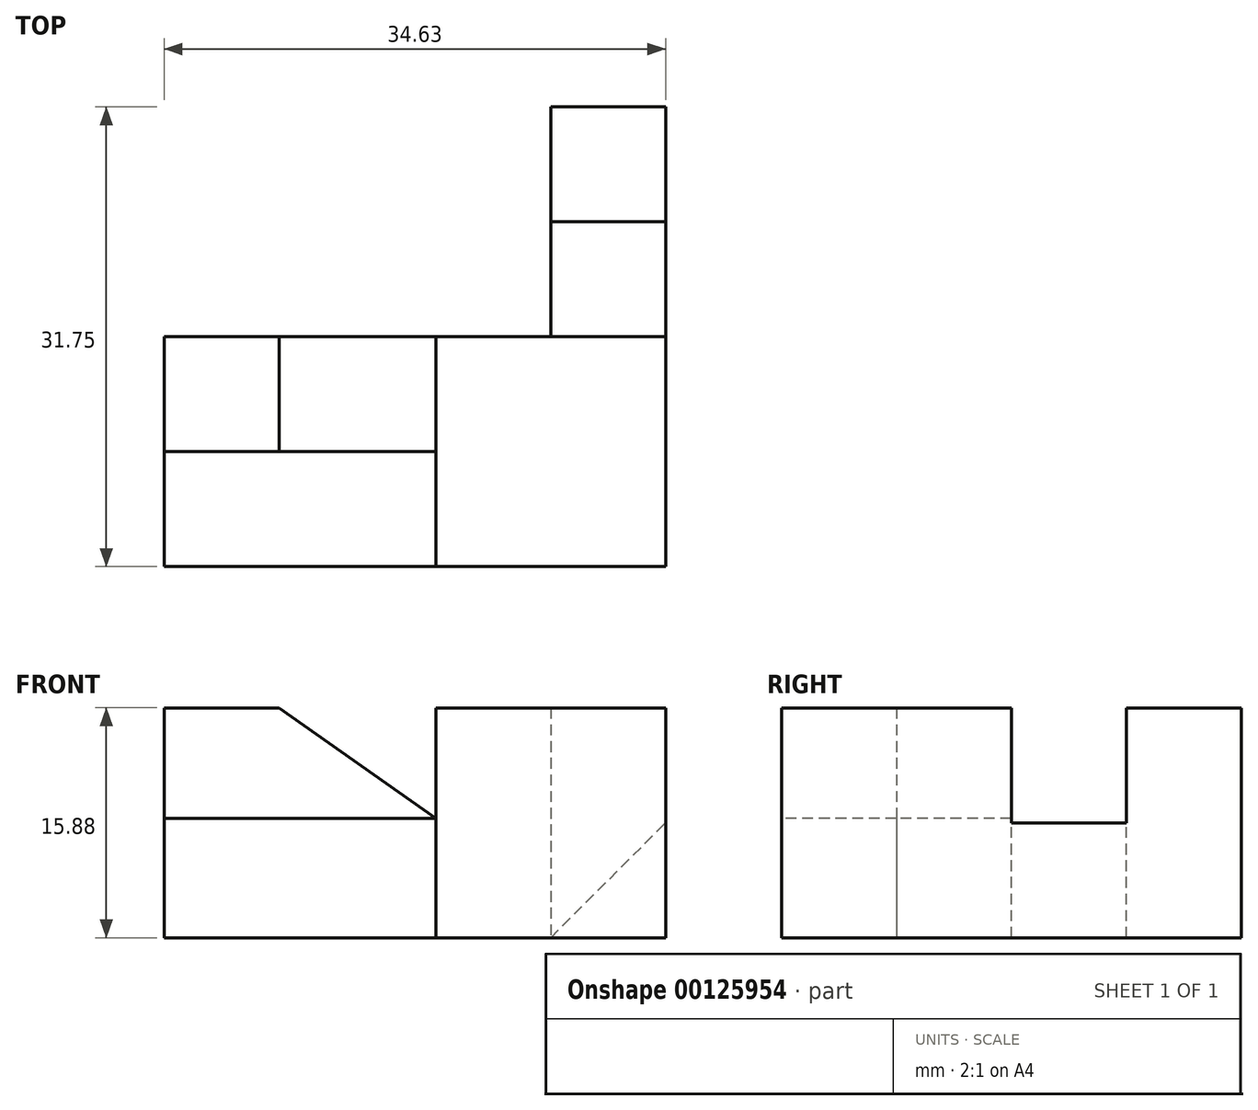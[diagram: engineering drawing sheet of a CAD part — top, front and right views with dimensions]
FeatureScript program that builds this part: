
annotation { "Feature Type Name" : "Feature", "Feature Type Description" : "" }
export const myFeature = defineFeature(function(context is Context, id is Id, definition is map)
    precondition{}
    {
        {
            var Q0;
            Q0=qCreatedBy(makeId("Top.planeOp"),FACE);
            var sketch = newSketch(context, id + "F0", { "sketchPlane" : qUnion([Q0])});
            skLineSegment(sketch, "E0.bottom", {"start": v(0, 0) * mm, "end": v(34.63, 0) * mm});
            skLineSegment(sketch, "E0.right", {"start": v(34.63, 0) * mm, "end": v(34.63, 31.75) * mm});
            skLineSegment(sketch, "E1", {"start": v(0, 15.88) * mm, "end": v(34.63, 15.88) * mm});
            skLineSegment(sketch, "E2", {"start": v(7.94, 15.88) * mm, "end": v(7.94, 7.94) * mm});
            skLineSegment(sketch, "E3", {"start": v(0, 15.88) * mm, "end": v(0, 0) * mm});
            skLineSegment(sketch, "E4", {"start": v(26.7, 31.75) * mm, "end": v(34.63, 31.75) * mm});
            skLineSegment(sketch, "E5", {"start": v(26.7, 23.81) * mm, "end": v(34.63, 23.81) * mm});
            skLineSegment(sketch, "E6", {"start": v(18.75, 15.88) * mm, "end": v(18.75, 0) * mm});
            skLineSegment(sketch, "E7", {"start": v(26.7, 31.75) * mm, "end": v(26.7, 15.88) * mm});
            skLineSegment(sketch, "E8", {"start": v(0, 7.94) * mm, "end": v(18.75, 7.94) * mm});
            skSolve(sketch);
        }
        {
            var Q0;
            {var subQ3=sQuery(id+"F0.wireOp",EDGE,"E2");Q0=makeQuery(id+"F0.imprint","IMPRINT",FACE,{"disambiguationData":[TD([[makeQuery(id+"F0.imprint","IMPRINT",EDGE,{"derivedFrom":subQ3}),-1.0]])]});}
            var Q1;
            {var subQ0=sQuery(id+"F0.wireOp",EDGE,"E2");Q1=makeQuery(id+"F0.imprint","IMPRINT",FACE,{"disambiguationData":[TD([[makeQuery(id+"F0.imprint","IMPRINT",EDGE,{"derivedFrom":subQ0}),1.0]])]});}
            var Q2;
            {var subQ3=sQuery(id+"F0.wireOp",EDGE,"E5");Q2=makeQuery(id+"F0.imprint","IMPRINT",FACE,{"disambiguationData":[TD([[makeQuery(id+"F0.imprint","IMPRINT",EDGE,{"derivedFrom":subQ3}),-1.0]])]});}
            var Q3;
            {var subQ1=sQuery(id+"F0.wireOp",EDGE,"E0.right");var subQ4=sQuery(id+"F0.wireOp",EDGE,"E0.bottom");var subQ5=makeQuery(id+"F0.imprint","INTERSECT",VERTEX,{"derivedFrom":[subQ4,subQ1]});Q3=makeQuery(id+"F0.imprint","IMPRINT",FACE,{"disambiguationData":[TD([[makeQuery(id+"F0.imprint","IMPRINT",EDGE,{"disambiguationData":[TD([[subQ5,1.0]])],"derivedFrom":subQ4}),1.0]])]});}
            var Q4;
            {var subQ0=sQuery(id+"F0.wireOp",EDGE,"E4");Q4=makeQuery(id+"F0.imprint","IMPRINT",FACE,{"disambiguationData":[TD([[makeQuery(id+"F0.imprint","IMPRINT",EDGE,{"derivedFrom":subQ0}),-1.0]])]});}
            extrude(context, id + "F1", {"entities" : qUnion([Q0, Q1, Q2, Q3, Q4]), "depth" : 15.88 * mm});
        }
        {
            var Q0;
            Q0=makeQuery(id+"F1.opExtrude","SWEPT_FACE",FACE,{"disambiguationData":[OSD([sQuery(id+"F0.wireOp",EDGE,"E0.right")])]});
            var sketch = newSketch(context, id + "F2", { "sketchPlane" : qUnion([Q0])});
            skLineSegment(sketch, "E9", {"start": v(15.87, 0) * mm, "end": v(15.87, 15.88) * mm});
            skLineSegment(sketch, "E10.0", {"start": v(0, 0) * mm, "end": v(31.75, 0) * mm});
            skLineSegment(sketch, "E11.0", {"start": v(0, 15.88) * mm, "end": v(31.75, 15.88) * mm});
            skLineSegment(sketch, "E12", {"start": v(23.81, 0) * mm, "end": v(23.81, 15.88) * mm});
            skLineSegment(sketch, "E13", {"start": v(15.87, 7.94) * mm, "end": v(23.81, 7.94) * mm});
            skSolve(sketch);
        }
        {
            var Q0;
            {var subQ3=sQuery(id+"F2.wireOp",EDGE,"E13");Q0=makeQuery(id+"F2.imprint","IMPRINT",FACE,{"disambiguationData":[TD([[makeQuery(id+"F2.imprint","IMPRINT",EDGE,{"derivedFrom":subQ3}),1.0]])]});}
            extrude(context, id + "F3", {"entities" : qUnion([Q0]), "operationType" : NewBodyOperationType.REMOVE, "oppositeDirection" : true, "depth" : 25.4 * mm});
        }
        {
            var Q0;
            Q0=makeQuery(id+"F3.boolean.opBoolean","COPY",FACE,{"derivedFrom":makeQuery(id+"F3.opExtrude","SWEPT_FACE",FACE,{"disambiguationData":[OSD([sQuery(id+"F2.wireOp",EDGE,"E13")])]})});
            extrude(context, id + "F4", {"entities" : qUnion([Q0]), "operationType" : NewBodyOperationType.REMOVE, "oppositeDirection" : true, "depth" : 25 * mm});
        }
        {
            var Q0;
            {var subQ0=sQuery(id+"F2.wireOp",EDGE,"E12");Q0=makeQuery(id+"F4.boolean.opBoolean","MERGE",FACE,{"derivedFrom":[makeQuery(id+"F3.boolean.opBoolean","COPY",FACE,{"derivedFrom":makeQuery(id+"F3.opExtrude","SWEPT_FACE",FACE,{"disambiguationData":[OSD([subQ0])]})}),makeQuery(id+"F4.opExtrude","SWEPT_FACE",FACE,{"disambiguationData":[OSD([subQ0,sQuery(id+"F2.wireOp",EDGE,"E13")])]})]});}
            var sketch = newSketch(context, id + "F5", { "sketchPlane" : qUnion([Q0])});
            skLineSegment(sketch, "E14", {"start": v(26.7, 7.94) * mm, "end": v(34.63, 7.94) * mm});
            skLineSegment(sketch, "E15", {"start": v(26.7, 0) * mm, "end": v(34.63, 7.94) * mm});
            skSolve(sketch);
        }
        {
            var Q0;
            {var subQ0=sQuery(id+"F5.wireOp",EDGE,"E15");Q0=makeQuery(id+"F5.imprint","IMPRINT",FACE,{"disambiguationData":[TD([[makeQuery(id+"F5.imprint","IMPRINT",EDGE,{"derivedFrom":subQ0}),-1.0]])]});}
            extrude(context, id + "F6", {"entities" : qUnion([Q0]), "operationType" : NewBodyOperationType.ADD, "depth" : 7.98 * mm});
        }
        {
            var Q0;
            {var subQ1=sQuery(id+"F0.wireOp",EDGE,"E0.bottom");var subQ5=sQuery(id+"F0.wireOp",EDGE,"E3");var subQ6=makeQuery(id+"F0.imprint","INTERSECT",VERTEX,{"derivedFrom":[subQ1,subQ5]});Q0=makeQuery(id+"F0.imprint","IMPRINT",FACE,{"disambiguationData":[TD([[makeQuery(id+"F0.imprint","IMPRINT",EDGE,{"disambiguationData":[TD([[subQ6,-1.0]])],"derivedFrom":subQ1}),1.0]])]});}
            extrude(context, id + "F7", {"entities" : qUnion([Q0]), "depth" : 8.25 * mm});
        }
        {
            var Q0;
            Q0=makeQuery(id+"F1.opExtrude","SWEPT_FACE",FACE,{"disambiguationData":[OSD([sQuery(id+"F0.wireOp",EDGE,"E8")])]});
            var sketch = newSketch(context, id + "F8", { "sketchPlane" : qUnion([Q0])});
            skLineSegment(sketch, "E16.0", {"start": v(0, 15.88) * mm, "end": v(18.75, 15.88) * mm});
            skLineSegment(sketch, "E17.0", {"start": v(0, 8.26) * mm, "end": v(18.75, 8.26) * mm});
            skLineSegment(sketch, "E18", {"start": v(7.94, 15.88) * mm, "end": v(7.94, 8.26) * mm});
            skLineSegment(sketch, "E19", {"start": v(7.94, 15.88) * mm, "end": v(18.75, 8.26) * mm});
            skSolve(sketch);
        }
        {
            var Q0;
            {var subQ3=sQuery(id+"F8.wireOp",EDGE,"E19");Q0=makeQuery(id+"F8.imprint","IMPRINT",FACE,{"disambiguationData":[TD([[makeQuery(id+"F8.imprint","IMPRINT",EDGE,{"derivedFrom":subQ3}),1.0]])]});}
            extrude(context, id + "F9", {"entities" : qUnion([Q0]), "operationType" : NewBodyOperationType.REMOVE, "oppositeDirection" : true, "depth" : 25 * mm});
        }
    });
